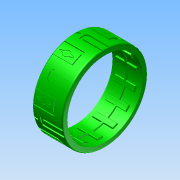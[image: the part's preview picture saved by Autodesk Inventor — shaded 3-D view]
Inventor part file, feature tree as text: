
AUTODESK INVENTOR PART (.ipt)
format: ipt  version: 2014 (Build 180170000, 170)  size: 2,141,184 bytes
history: native  units: in
note: dims shown in document units (in); Inventor stores cm internally (conversion verified against a paired STEP export)
features: fillet x3, sketch x2, revolve x2, pattern_circular x2, plane x1, emboss x1
ambient origin geometry x8: Origin, YZ Plane, XZ Plane, XY Plane, X Axis, Y Axis, Z Axis, Center Point
bodies: Solid1 (feature_tree)
feature tree (11):
  sketch  "Sketch1"  dims[d0=1.65in d1=1.45in]
  revolve  "Revolution1"  [1 undecoded]
  revolve  "Revolution2"  [1 undecoded]
  plane  "Work Plane1"
  fillet  "Fillet1"  Radius=0.3534in
  emboss  "Emboss1"
  fillet  "Fillet2"  Radius=0.05in
  pattern_circular  "Circular Pattern1"  [2 undecoded]
  fillet  "Fillet3"  Radius=0.3in
  pattern_circular  "Circular Pattern2"  [2 undecoded]
  sketch  "Sketch2"  dims[d2=0.58in d3=0.03in d4=0.3534in d5=0.05in d6=0.05in d12=0.3in d15=0.03in d17=0.05in d18=0.2in d25=0.02in d26=0.0in d27=0.05in d28=0.02in d29=0.01in d30=2.7559in d31=360.0deg d33=0.14in d35=0.57in d36=0.08in d37=0.05in d38=0.01in d39=0.13in d40=0.05in d41=0.05in d42=0.4in d43=0.055in d44=0.01in d45=5.9055in d46=360.0deg]
note: 6 required parameter values undecoded (feature->parameter linkage not recoverable at this tier; creation-order binding heuristic only, values carry confidence <= 0.55)